# Revit family: 940-0006_0007_0012_0013
name_source: partatom
category: Mechanical Equipment
revit_build: Autodesk Revit 2013 (Build: 20120221_2030(x64)
units: mm (PartAtom-declared; Revit-internal decimal feet)

## types (4) — shared parameters
Alarm Panel = Nema 4X Polycarbonate
Alarm Panel Cd Length = 120"
Alarm Panel Dimensions = 6" X 6" X 4"
Assembly Code = D2010900
Default Elevation = 0"
Description = Oil Guard Pump Switch and Panel
High Liquid Alarm Switch = High Impact Plastic
High Liquid Alarm Switch Cd Length = 240"
High Liquid Alarm Switch Dimensions = 1.5" w X 3.5" h X 1.5" d
Installation Type = Floor Mounted
Manufacturer = Zoeller
Masterformat Number = 33 36 16
Masterformat Title = Utility Septic Tank Effluent Pumps
Omniclass Table 23 Code = 23.60.30.21
Omniclass Table 23 Title = Pumps
Phase = 1
Price = Prices may vary. Please consult Manufacturer Representative for most up-to-date price list.
Product Page URL = http://www.zoellerpumps.com
Pump = Cast Iron-Zoeller-Powder Coated Epoxy
Pump Discharge Diameter = 1 1/2"
Pump Height = 12 1/8"
Pump Length = 10 3/32"
Pump Switch = High Impact Plastic
Pump Switch Cd Length (Piggyback) = 240"
Pump Switch Dimensions = 2.5" w X 6" h X 1.75" d
Pump Switch Family = Oil_Smart_System-Zoeller-Pipe_Assembly : Discharge_Pipe_Assembly_With_Plug
Pump Switch Sensor Probe = 6"
Pump Width = 7 3/4"
URL = http://www.zoellerpumps.com
Voltage = 115 V
Waste Connection = Yes

## per-type parameters (varying)
| type | Max Flow @ 5' Hd | Maximum Head | Pump Amps | Pump Cord Length | Pump Family | Pump HP | SO Jacketed Cord (Oil Resistant) |
| 940-0007 | 77 GPM | 528" | 10.5 | 6' | Pump_Commercial-Effluent-Zoeller-152-153 : 153 | 1/2 HP | No |
| 940-0006 | 69 GPM | 456" | 8.5 | 6' | Pump_Commercial-Effluent-Zoeller-152-153 : 152 | 4/10 HP | No |
| 940-0012 | 69 GPM | 456" | 8.5 | 6' or 72" | Pump_Commercial-Effluent-Zoeller-152-153 : 152 | 4/10 HP | Yes |
| 940-0013 | 77 GPM | 528" | 10.5 | 6' or 72" | Pump_Commercial-Effluent-Zoeller-152-153 : 153 | 1/2 HP | Yes |

note: column(s) folded — value = type name in every type: Model

## geometry (parser evidence)
native form markers: Blend x8, Sweep x11
no freeform markers — native parametric forms only
